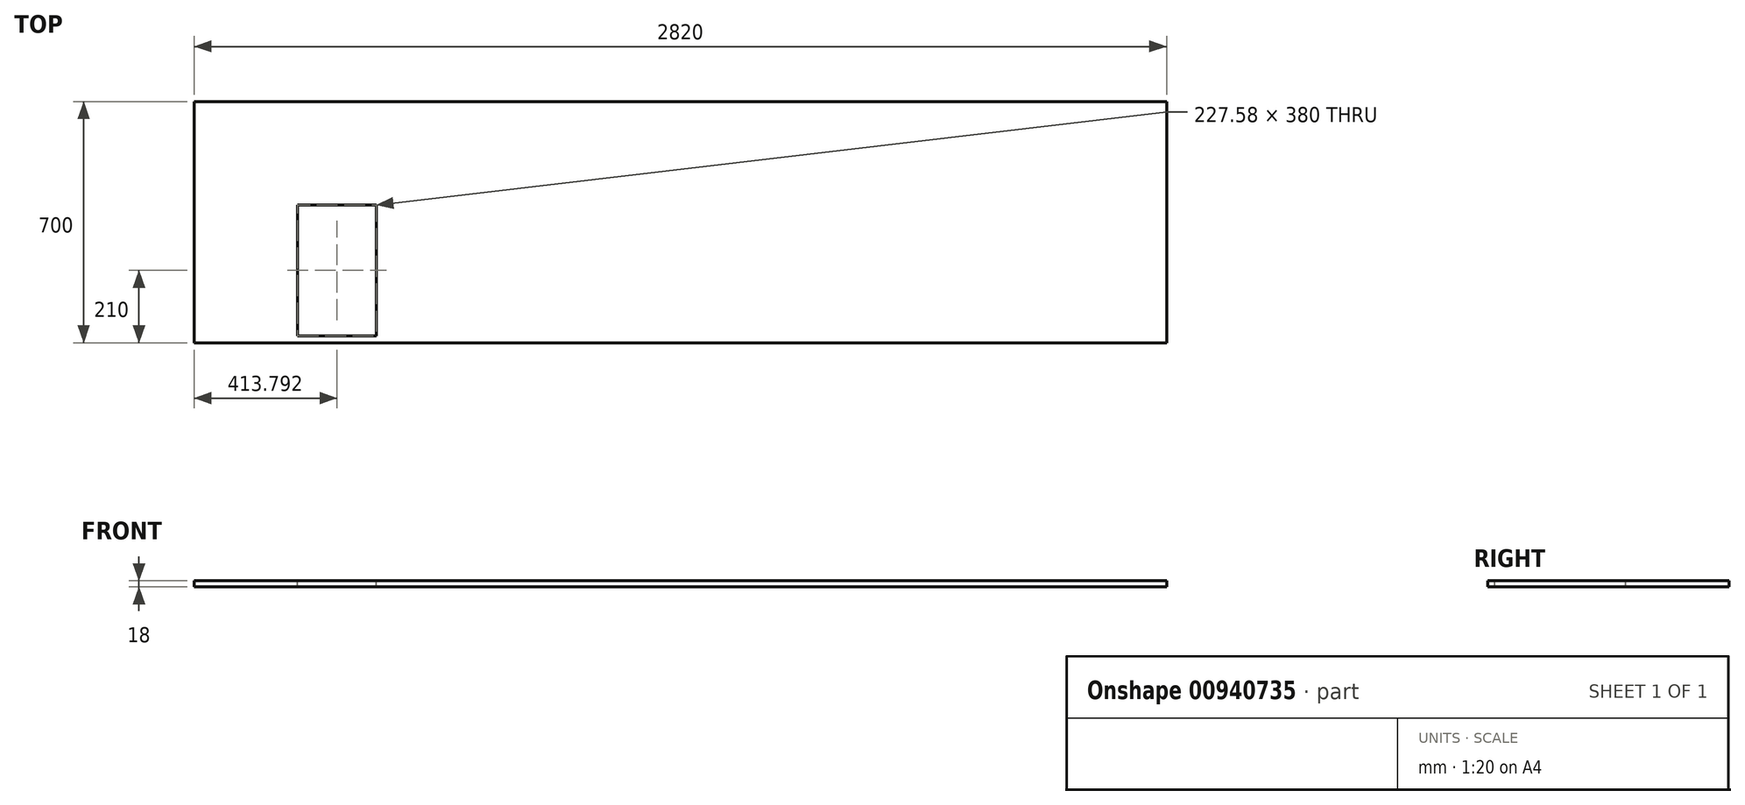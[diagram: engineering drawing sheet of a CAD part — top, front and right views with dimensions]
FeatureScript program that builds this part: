
annotation { "Feature Type Name" : "Feature", "Feature Type Description" : "" }
export const myFeature = defineFeature(function(context is Context, id is Id, definition is map)
    precondition{}
    {
        {
            var Q0;
            Q0=qCreatedBy(makeId("Top.planeOp"),FACE);
            var sketch = newSketch(context, id + "F0", { "sketchPlane" : qUnion([Q0])});
            skLineSegment(sketch, "E0.bottom", {"start": v(1410, -350) * mm, "end": v(-1410, -350) * mm});
            skLineSegment(sketch, "E0.top", {"start": v(1410, 350) * mm, "end": v(-1410, 350) * mm});
            skLineSegment(sketch, "E0.left", {"start": v(1410, -350) * mm, "end": v(1410, 350) * mm});
            skLineSegment(sketch, "E0.right", {"start": v(-1410, -350) * mm, "end": v(-1410, 350) * mm});
            skPoint(sketch, "E0.middle", {"position": v(0, 0) * mm});
            skSolve(sketch);
        }
        {
            var Q0;
            Q0=makeQuery(id+"F0.imprint","IMPRINT",FACE,{"disambiguationData":[TD([[makeQuery(id+"F0.imprint","IMPRINT",EDGE,{"derivedFrom":sQuery(id+"F0.wireOp",EDGE,"E0.bottom")}),-1.0]])]});
            extrude(context, id + "F1", {"entities" : qUnion([Q0]), "endBound" : BoundingType.SYMMETRIC, "depth" : 18 * mm, "offsetDistance" : 25 * mm});
        }
        {
            var Q0;
            Q0=makeQuery(id+"F1.opExtrude","CAP_FACE",FACE,{"disambiguationData":[OSD([sQuery(id+"F0.wireOp",EDGE,"E0.bottom"),sQuery(id+"F0.wireOp",EDGE,"E0.top"),sQuery(id+"F0.wireOp",EDGE,"E0.left"),sQuery(id+"F0.wireOp",EDGE,"E0.right")])],"isStart":false});
            var sketch = newSketch(context, id + "F2", { "sketchPlane" : qUnion([Q0])});
            skLineSegment(sketch, "E1.bottom", {"start": v(-1110, 50) * mm, "end": v(-882.42, 50) * mm});
            skLineSegment(sketch, "E1.top", {"start": v(-1110, -330) * mm, "end": v(-882.42, -330) * mm});
            skLineSegment(sketch, "E1.left", {"start": v(-1110, 50) * mm, "end": v(-1110, -330) * mm});
            skLineSegment(sketch, "E1.right", {"start": v(-882.42, 50) * mm, "end": v(-882.42, -330) * mm});
            skSolve(sketch);
        }
        {
            var Q0;
            Q0 = qSketchRegion(id + "F2", true);
            extrude(context, id + "F3", {"entities" : qUnion([Q0]), "operationType" : NewBodyOperationType.REMOVE, "oppositeDirection" : true, "depth" : 25 * mm, "offsetDistance" : 25 * mm});
        }
    });
